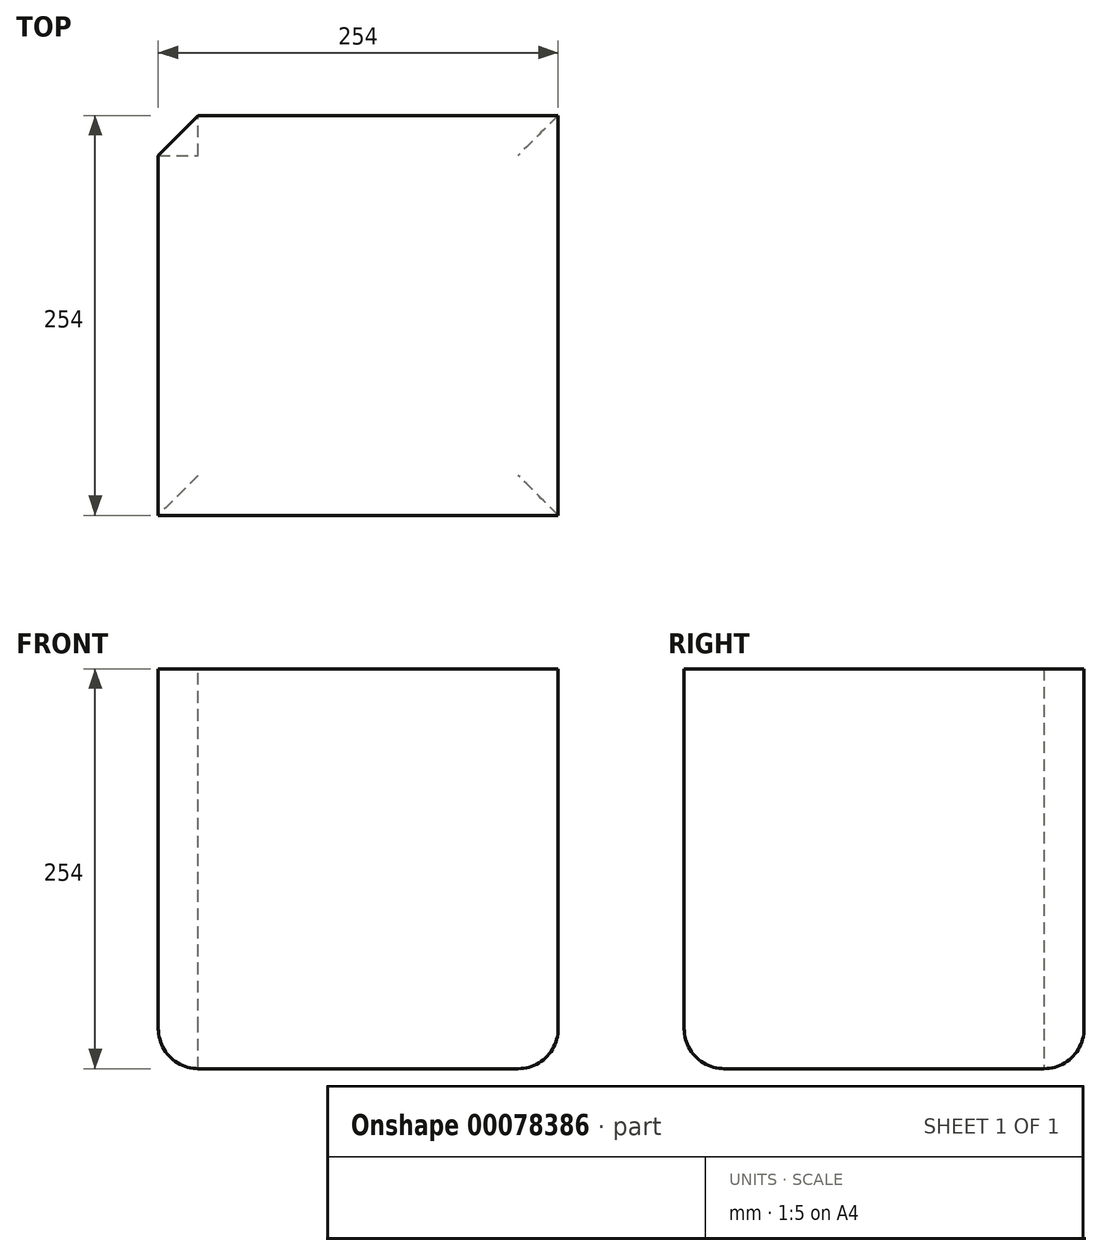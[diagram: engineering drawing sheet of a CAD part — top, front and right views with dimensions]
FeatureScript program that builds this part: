
annotation { "Feature Type Name" : "Feature", "Feature Type Description" : "" }
export const myFeature = defineFeature(function(context is Context, id is Id, definition is map)
    precondition{}
    {
        {
            var Q0;
            Q0=qCreatedBy(makeId("Front.planeOp"),FACE);
            var sketch = newSketch(context, id + "F0", { "sketchPlane" : qUnion([Q0])});
            skLineSegment(sketch, "E0", {"start": v(127, 127) * mm, "end": v(-127, 127) * mm});
            skLineSegment(sketch, "E1", {"start": v(-127, 127) * mm, "end": v(-127, -127) * mm});
            skLineSegment(sketch, "E2", {"start": v(-127, -127) * mm, "end": v(127, -127) * mm});
            skLineSegment(sketch, "E3", {"start": v(127, -127) * mm, "end": v(127, 127) * mm});
            skSolve(sketch);
        }
        {
            var Q0;
            Q0=makeQuery(id+"F0.imprint","IMPRINT",FACE,{"disambiguationData":[TD([[makeQuery(id+"F0.imprint","IMPRINT",EDGE,{"derivedFrom":sQuery(id+"F0.wireOp",EDGE,"E0")}),1.0]])]});
            extrude(context, id + "F1", {"entities" : qUnion([Q0]), "depth" : 254 * mm});
        }
        {
            var Q0;
            Q0=makeQuery(id+"F1.opExtrude","SWEPT_FACE",FACE,{"disambiguationData":[OSD([sQuery(id+"F0.wireOp",EDGE,"E2")])]});
            fillet(context, id + "F2", {"entities" : qUnion([Q0]), "radius" : 25.4 * mm, "tangentPropagation" : true, "allowEdgeOverflow" : false});
        }
        {
            var Q0;
            Q0=makeQuery(id+"F1.opExtrude","CAP_EDGE",EDGE,{"disambiguationData":[OSD([sQuery(id+"F0.wireOp",EDGE,"E1")])],"isStart":true});
            chamfer(context, id + "F3", {"entities" : qUnion([Q0]), "width" : 25.4 * mm, "tangentPropagation" : true});
        }
    });
